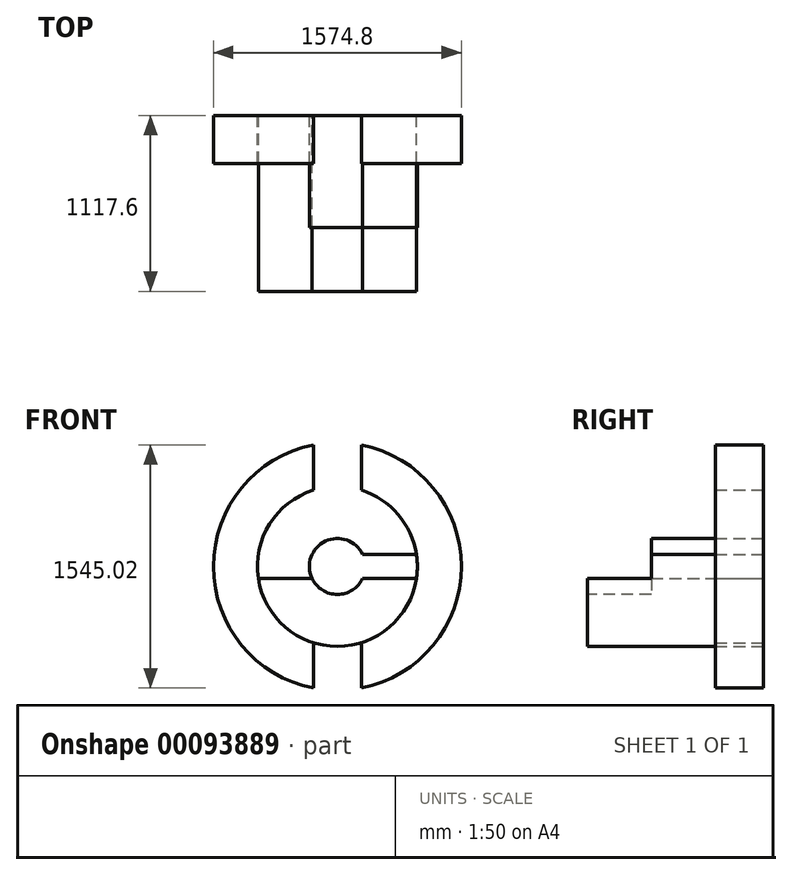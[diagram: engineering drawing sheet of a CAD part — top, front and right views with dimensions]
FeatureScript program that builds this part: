
annotation { "Feature Type Name" : "Feature", "Feature Type Description" : "" }
export const myFeature = defineFeature(function(context is Context, id is Id, definition is map)
    precondition{}
    {
        {
            var Q0;
            Q0=qCreatedBy(makeId("Front.planeOp"),FACE);
            var sketch = newSketch(context, id + "F0", { "sketchPlane" : qUnion([Q0])});
            skCircle(sketch, "E0", {"center": v(0, 0) * mm, "radius": 787.4 * mm});
            skCircle(sketch, "E1", {"center": v(0, 0) * mm, "radius": 508 * mm});
            skCircle(sketch, "E2", {"center": v(0, 0) * mm, "radius": 177.8 * mm});
            skLineSegment(sketch, "E3", {"start": v(0, 787.4) * mm, "end": v(0, 508) * mm, "construction": true});
            skLineSegment(sketch, "E4", {"start": v(-508, 0) * mm, "end": v(-177.8, 0) * mm, "construction": true});
            skLineSegment(sketch, "E5", {"start": v(152.4, 772.51) * mm, "end": v(152.4, 484.6) * mm});
            skLineSegment(sketch, "E6", {"start": v(-502.25, 76.2) * mm, "end": v(-160.64, 76.2) * mm});
            skLineSegment(sketch, "E7.MirrorCS", {"start": v(-152.4, 772.51) * mm, "end": v(-152.4, 484.6) * mm});
            skLineSegment(sketch, "E8.MirrorCS", {"start": v(502.25, 76.2) * mm, "end": v(160.64, 76.2) * mm});
            skLineSegment(sketch, "E9.MirrorCS", {"start": v(502.25, -76.2) * mm, "end": v(160.64, -76.2) * mm});
            skLineSegment(sketch, "E10.trimOffspring", {"start": v(-160.64, 76.2) * mm, "end": v(-502.25, 76.2) * mm});
            skLineSegment(sketch, "E11.trimOffspring", {"start": v(177.8, 0) * mm, "end": v(508, 0) * mm, "construction": true});
            skPoint(sketch, "E12.orphan", {"position": v(-508, 0) * mm});
            skPoint(sketch, "E13.orphan", {"position": v(508, 0) * mm});
            skLineSegment(sketch, "E14.trimOffspring", {"start": v(-160.64, -76.2) * mm, "end": v(-502.25, -76.2) * mm});
            skLineSegment(sketch, "E15.trimOffspring", {"start": v(-152.4, -484.6) * mm, "end": v(-152.4, -772.51) * mm});
            skLineSegment(sketch, "E16.trimOffspring", {"start": v(152.4, -484.6) * mm, "end": v(152.4, -772.51) * mm});
            skLineSegment(sketch, "E17.trimOffspring", {"start": v(160.64, 76.2) * mm, "end": v(502.25, 76.2) * mm});
            skSolve(sketch);
        }
        {
            var Q0;
            {var subQ0=sQuery(id+"F0.wireOp",EDGE,"E10.trimOffspring");Q0=makeQuery(id+"F0.imprint","IMPRINT",FACE,{"disambiguationData":[TD([[makeQuery(id+"F0.imprint","IMPRINT",EDGE,{"derivedFrom":subQ0}),-1.0]])]});}
            var Q1;
            {var subQ0=sQuery(id+"F0.wireOp",EDGE,"E10.trimOffspring");Q1=makeQuery(id+"F0.imprint","IMPRINT",FACE,{"disambiguationData":[TD([[makeQuery(id+"F0.imprint","IMPRINT",EDGE,{"derivedFrom":subQ0}),1.0]])]});}
            var Q2;
            {var subQ0=sQuery(id+"F0.wireOp",EDGE,"E2");var subQ1=makeQuery(id+"F0.imprint","INTERSECT",VERTEX,{"derivedFrom":[subQ0,sQuery(id+"F0.wireOp",EDGE,"E10.trimOffspring")]});Q2=makeQuery(id+"F0.imprint","IMPRINT",FACE,{"disambiguationData":[TD([[makeQuery(id+"F0.imprint","IMPRINT",EDGE,{"disambiguationData":[TD([[subQ1,1.0]])],"derivedFrom":subQ0}),1.0]])]});}
            var Q3;
            {var subQ0=sQuery(id+"F0.wireOp",EDGE,"E9.MirrorCS");Q3=makeQuery(id+"F0.imprint","IMPRINT",FACE,{"disambiguationData":[TD([[makeQuery(id+"F0.imprint","IMPRINT",EDGE,{"derivedFrom":subQ0}),-1.0]])]});}
            var Q4;
            {var subQ0=sQuery(id+"F0.wireOp",EDGE,"E9.MirrorCS");Q4=makeQuery(id+"F0.imprint","IMPRINT",FACE,{"disambiguationData":[TD([[makeQuery(id+"F0.imprint","IMPRINT",EDGE,{"derivedFrom":subQ0}),1.0]])]});}
            extrude(context, id + "F1", {"entities" : qUnion([Q0, Q1, Q2, Q3, Q4]), "depth" : 1117.6 * mm});
        }
        {
            var Q0;
            {var subQ3=sQuery(id+"F0.wireOp",EDGE,"E7.MirrorCS");Q0=makeQuery(id+"F0.imprint","IMPRINT",FACE,{"disambiguationData":[TD([[makeQuery(id+"F0.imprint","IMPRINT",EDGE,{"derivedFrom":subQ3}),-1.0]])]});}
            var Q1;
            {var subQ4=sQuery(id+"F0.wireOp",EDGE,"E5");Q1=makeQuery(id+"F0.imprint","IMPRINT",FACE,{"disambiguationData":[TD([[makeQuery(id+"F0.imprint","IMPRINT",EDGE,{"derivedFrom":subQ4}),1.0]])]});}
            extrude(context, id + "F2", {"entities" : qUnion([Q0, Q1]), "operationType" : NewBodyOperationType.ADD, "depth" : 304.8 * mm});
        }
        {
            var Q0;
            Q0=makeQuery(id+"F1.opExtrude","CAP_FACE",FACE,{"disambiguationData":[OSD([sQuery(id+"F0.wireOp",EDGE,"E1")])],"isStart":false});
            var sketch = newSketch(context, id + "F3", { "sketchPlane" : qUnion([Q0])});
            skCircle(sketch, "E18.0", {"center": v(0, 0) * mm, "radius": 177.8 * mm});
            skLineSegment(sketch, "E19.0", {"start": v(-160.64, 76.2) * mm, "end": v(-502.25, 76.2) * mm});
            skLineSegment(sketch, "E20.0", {"start": v(-160.64, -76.2) * mm, "end": v(-502.25, -76.2) * mm});
            skLineSegment(sketch, "E21.0", {"start": v(502.25, 76.2) * mm, "end": v(160.64, 76.2) * mm});
            skLineSegment(sketch, "E22.0", {"start": v(502.25, -76.2) * mm, "end": v(160.64, -76.2) * mm});
            skCircle(sketch, "E23.0", {"center": v(0, 0) * mm, "radius": 508 * mm});
            skSolve(sketch);
        }
        {
            var Q0;
            {var subQ0=sQuery(id+"F3.wireOp",EDGE,"E19.0");Q0=makeQuery(id+"F3.imprint","IMPRINT",FACE,{"disambiguationData":[TD([[makeQuery(id+"F3.imprint","IMPRINT",EDGE,{"derivedFrom":subQ0}),1.0]])]});}
            var Q1;
            {var subQ0=sQuery(id+"F3.wireOp",EDGE,"E18.0");var subQ1=makeQuery(id+"F3.imprint","INTERSECT",VERTEX,{"derivedFrom":[subQ0,sQuery(id+"F3.wireOp",EDGE,"E21.0")]});Q1=makeQuery(id+"F3.imprint","IMPRINT",FACE,{"disambiguationData":[TD([[makeQuery(id+"F3.imprint","IMPRINT",EDGE,{"disambiguationData":[TD([[subQ1,1.0]])],"derivedFrom":subQ0}),1.0]])]});}
            var Q2;
            {var subQ0=sQuery(id+"F3.wireOp",EDGE,"E21.0");Q2=makeQuery(id+"F3.imprint","IMPRINT",FACE,{"disambiguationData":[TD([[makeQuery(id+"F3.imprint","IMPRINT",EDGE,{"derivedFrom":subQ0}),1.0]])]});}
            extrude(context, id + "F4", {"entities" : qUnion([Q0, Q1, Q2]), "operationType" : NewBodyOperationType.REMOVE, "oppositeDirection" : true, "depth" : 406.4 * mm});
        }
    });
